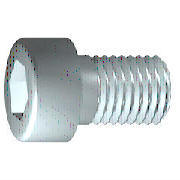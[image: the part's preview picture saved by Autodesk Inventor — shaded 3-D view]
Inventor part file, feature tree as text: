
AUTODESK INVENTOR PART (.ipt)
format: ipt  version: 2023.1 (Build 271208000, 208)  size: 208,384 bytes
history: native  units: mm (DEFAULTED — no unit token found)
features: sketch x2, extrude x1, plane x1, fillet x1
ambient origin geometry x7: Origin, YZ Plane, XY Plane, X Axis, Y Axis, Z Axis, Center Point
bodies: Solid1 (feature_tree), Body (feature_tree)
feature tree (5):
  extrude  "Slot"  Depth=3.0mm
  plane  "Work Plane1"
  fillet  "Fillet2"  Radius=3.0mm
  sketch  "Sketch1"  dims[d1=10.75mm d2=0.306825mm d3=3.0mm]
  sketch  "Sketch2"  dims[d4=1.3mm d5=60.0deg d6=3.0mm d7=3.0mm d8=2.886751mm d9=5.5mm d10=90.0deg d11=10.0mm d12=0.0mm d13=10.75mm d14=0.0mm d15=0.306725mm d16=0.306725mm d17=0.3mm d19=0.0mm d26=12.0mm d27=45.0deg d28=0.0mm d29=0.0mm d30=0.1mm]
